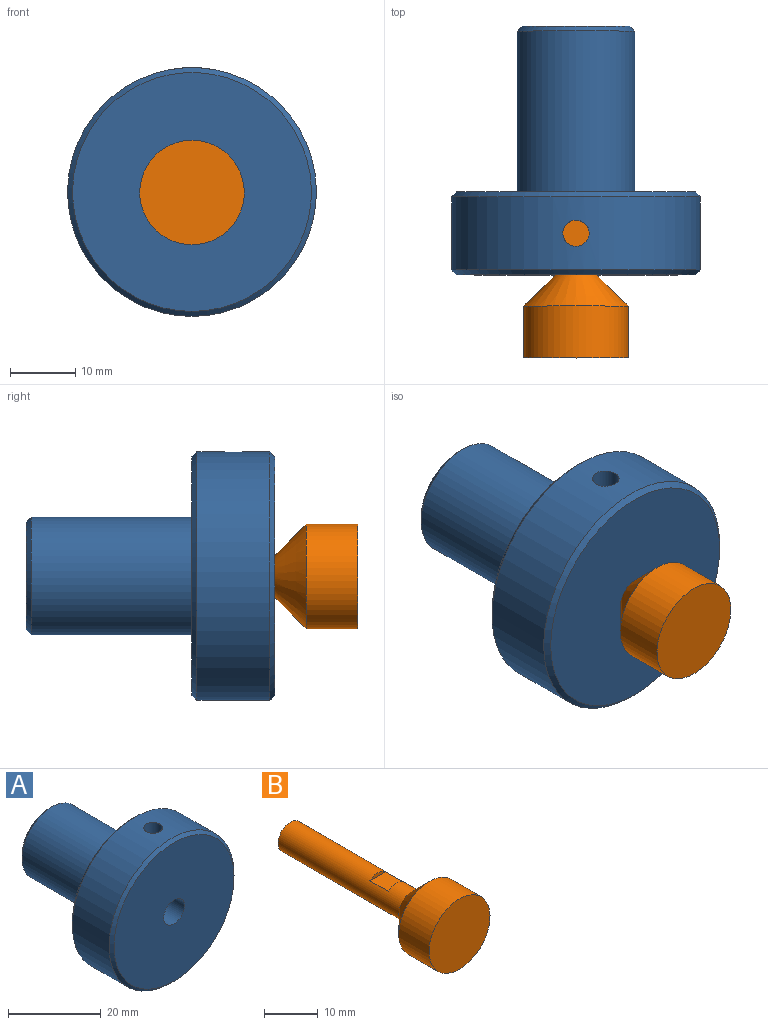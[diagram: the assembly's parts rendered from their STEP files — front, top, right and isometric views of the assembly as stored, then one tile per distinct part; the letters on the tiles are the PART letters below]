
ASSEMBLY  parts=2 mates=1
PART A: 10 faces, bbox 38.1x38.1x38.1 mm
  f0: cylinder r=3.17mm len=38.1mm, axis (0,-1,0), area 746.5mm2, adj f3,f5,f6
  f1: cylinder r=19.05mm len=38.1mm, axis (0,-1,0), area 1324.9mm2, adj f6,f8,f9
  f2: plane 36.58x36.58mm, normal (0,1,0), area 795.3mm2, adj f4,f8
  f3: plane 36.58x36.58mm, normal (0,-1,0), area 1019mm2, adj f0,f9
  f4: cylinder r=9.02mm len=24.64mm, axis (0,-1,0), area 1395.9mm2, adj f2,f7
  f5: plane 16.51x16.51mm, normal (0,1,0), area 182.4mm2, adj f0,f7
  f6: cylinder r=2.02mm len=16.6mm, axis (0,0,1), area 205.2mm2, adj f0,f1
  f7: cone r=8.26mm half-angle=45deg, axis (0,-1,0), area 58.5mm2, adj f4,f5
  f8: cone r=19.05mm half-angle=45deg, axis (0,-1,0), area 126.4mm2, adj f1,f2
  f9: cone r=18.29mm half-angle=45deg, axis (0,1,0), area 126.4mm2, adj f1,f3
PART B: 8 faces, bbox 16x44.5x16 mm
  f0: cylinder r=3.17mm len=31.75mm, axis (0,-1,0), area 611.9mm2, adj f3,f4,f5,f6,f7
  f1: cylinder r=8mm len=16mm, axis (0,-1,0), area 399mm2, adj f2,f3
  f2: plane 16x16mm, normal (0,-1,0), area 201.1mm2, adj f1
  f3: cone r=8mm half-angle=45.3deg, axis (0,-1,0), area 238.4mm2, adj f0,f1
  f4: plane 6.35x6.35mm, normal (0,1,0), area 31.7mm2, adj f0
  f5: plane 4.13x0.76mm, normal (0,-1,0), area 2.2mm2, adj f0,f7
  f6: plane 4.13x0.76mm, normal (0,1,0), area 2.2mm2, adj f0,f7
  f7: plane 4.78x4.13mm, normal (0,0,1), area 19.7mm2, adj f0,f5,f6
PLACE A t=(45.65,-1.03,-13.77)mm
PLACE B t=(45.65,-13.74,-13.84)mm
MATE fastened A.f6 <-> B.f7  axis (0,0,1) through (45.65,5.32,-11.43)mm
